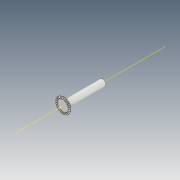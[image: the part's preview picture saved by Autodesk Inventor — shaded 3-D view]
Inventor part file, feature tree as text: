
AUTODESK INVENTOR PART (.ipt)
format: ipt  version: 2021 (Build 250183000, 183)  size: 506,368 bytes
history: native  units: mm
features: other x16, sketch x10, loft x3, pattern_circular x3, extrude x1
ambient origin geometry x6: Origin, XZ Plane, X Axis, Y Axis, Z Axis, Center Point
bodies: Solid1 (feature_tree)
feature tree (33):
  other  "Ponto superior"
  other  "Plano de malha 2"
  other  "Corpo dentado"
  other  "Ponto inicial"
  other  "Plano de dente"
  sketch  "Esboço inicial"  dims[d3=0.6mm]
  other  "Extremidade"
  loft  "Loft"
  pattern_circular  "Circular Pattern"  [2 undecoded]
  sketch  "Esboço 3D direito"  dims[d4=1.194087mm]
  other  "Plano final direito"
  loft  "Transição direita"
  pattern_circular  "Padrão circular direito"  Angle=90.0deg  [1 undecoded]
  sketch  "Esboço 3D esquerdo"  dims[d5=90.0deg]
  other  "Plano final esquerdo"
  loft  "Transição esquerda"
  pattern_circular  "Padrão circular esquerdo"  Angle=360.0deg  [1 undecoded]
  other  "Fixar corpo"
  extrude  "Extrusão1"  Depth=10.0mm
  other  "Plano de malha"
  other  "Plano superior"
  sketch  "Esboço de corpo dentado"  dims[d7=1.663639mm]
  other  "Plano final"
  sketch  "Esboço final"  dims[d8=1.691227mm]
  other  "Helical Curve Left"
  sketch  "Esboço final esquerdo"  dims[d9=4.071779mm]
  sketch  "Esboço de corpo"  dims[d11=0.6198mm]
  sketch  "Sketch6"  dims[d0=4.68mm d1=4.46412mm]
  other  "Srf1"
  other  "Helical Curve Right"
  sketch  "Esboço final direita"  dims[d12=1.281954mm d15=1.303212mm d16=3.137599mm d17=0.0mm d18=90.0deg d19=0.0mm d20=90.0deg d21=260.0mm d22=360.0deg d26=17.944705mm d27=0.309728mm d28=4.68mm d29=-10.47518mm d30=1.281954mm d31=1.303212mm d32=3.137599mm d35=0.0mm d37=0.0mm d39=0.0mm d40=90.0deg d41=260.0mm d42=360.0deg d46=90.0deg d47=90.0deg d48=0.0mm d49=0.0mm d50=90.0deg d51=1.208305mm d52=0.0mm d53=0.0mm d54=0.0mm d56=0.94732mm d57=4.981399mm d58=4.419079mm d59=3.838526mm d60=3.405218mm d61=3.838526mm d62=3.405218mm d65=17.944705mm d66=31.5mm d67=4.68mm d68=-10.47518mm d69=0.309728mm d70=1.303212mm d71=3.137599mm d72=1.281954mm d73=3.405218mm d74=3.838526mm d75=0.0mm d77=0.0mm d79=0.0mm d80=90.0deg d81=260.0mm d82=360.0deg d84=10.0mm d85=20.0mm d86=20.0mm d87=10.0mm d88=0.0mm d89=0.0mm d90=90.0deg d91=90.0deg d92=90.0deg d93=90.0deg d94=12.5mm d95=0.0mm]
  sketch  "Esboço8"  dims[d2=4.8599mm]
  other  "Diâmetro do flanco"
note: 4 required parameter values undecoded (feature->parameter linkage not recoverable at this tier; creation-order binding heuristic only, values carry confidence <= 0.55)
